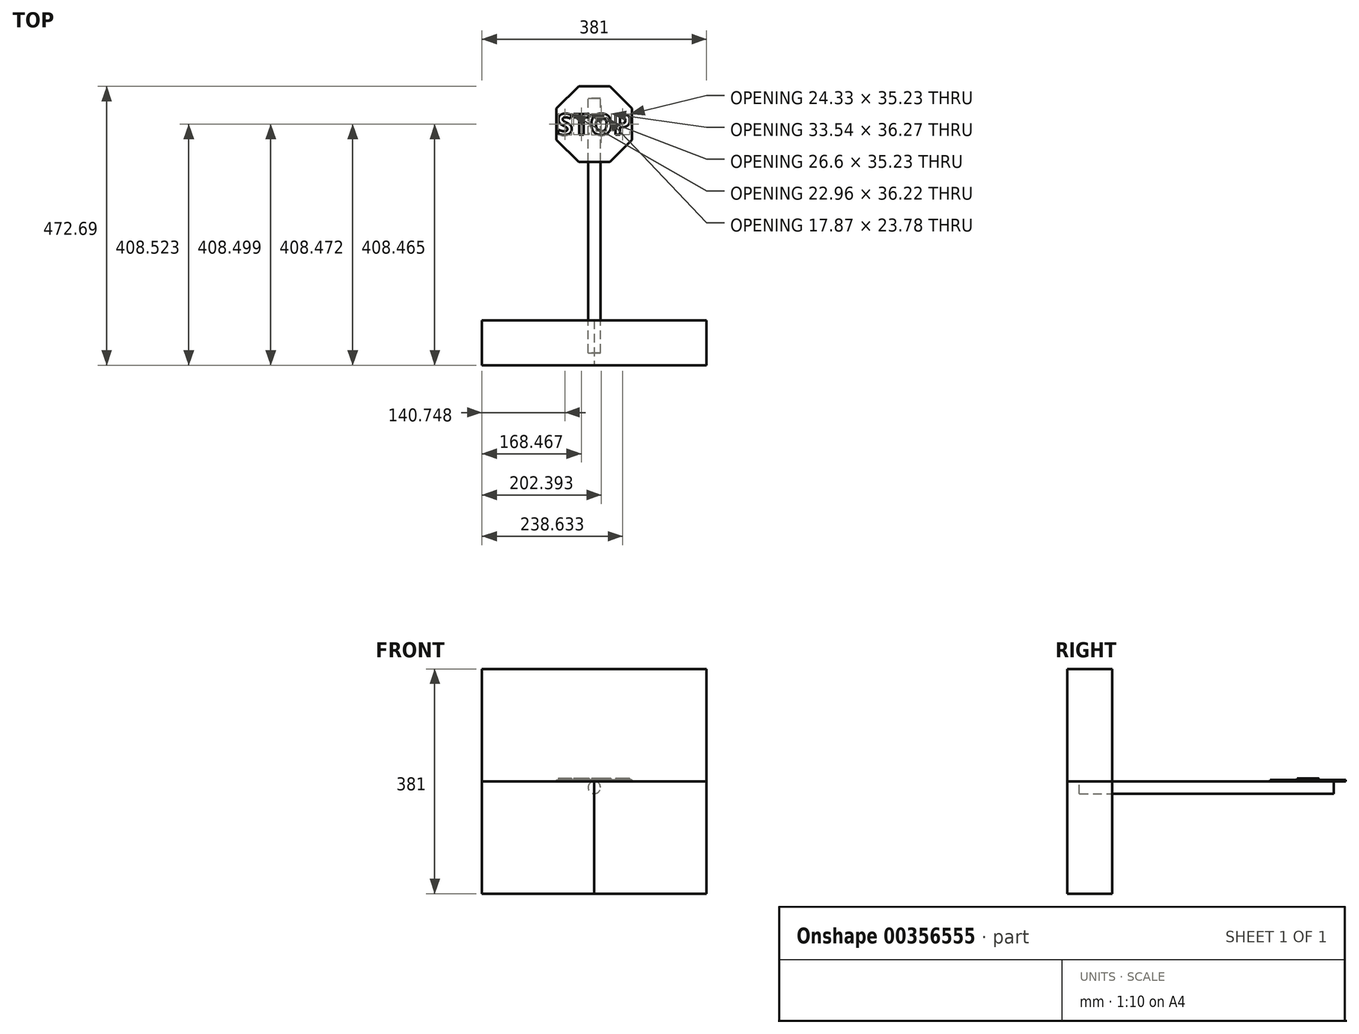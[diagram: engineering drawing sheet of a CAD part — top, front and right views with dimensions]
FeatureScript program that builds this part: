
annotation { "Feature Type Name" : "Feature", "Feature Type Description" : "" }
export const myFeature = defineFeature(function(context is Context, id is Id, definition is map)
    precondition{}
    {
        {
            var Q0;
            Q0=qCreatedBy(makeId("Top.planeOp"),FACE);
            var sketch = newSketch(context, id + "F0", { "sketchPlane" : qUnion([Q0])});
            skPoint(sketch, "E0.0.midPoint", {"position": v(0, -63.5) * mm});
            skText(sketch, "E1", { "text": "STOP\n\n", "fontName": "OpenSans-Bold.ttf"});
            skPoint(sketch, "E2.0.midPoint", {"position": v(-32.65, -98.94) * mm});
            skPoint(sketch, "E3.0.midPoint", {"position": v(-57.86, -79) * mm});
            skCircle(sketch, "E4.cCircle", {"center": v(0, -44.07) * mm, "radius": 64.08 * mm, "construction": true});
            skLineSegment(sketch, "E4.0", {"start": v(26.54, -108.15) * mm, "end": v(-26.54, -108.15) * mm});
            skLineSegment(sketch, "E4.1", {"start": v(-26.54, -108.15) * mm, "end": v(-64.08, -70.61) * mm});
            skLineSegment(sketch, "E4.2", {"start": v(-64.08, -70.61) * mm, "end": v(-64.08, -17.52) * mm});
            skLineSegment(sketch, "E4.3", {"start": v(-64.08, -17.52) * mm, "end": v(-26.54, 20.01) * mm});
            skLineSegment(sketch, "E4.4", {"start": v(-26.54, 20.01) * mm, "end": v(26.54, 20.01) * mm});
            skLineSegment(sketch, "E4.5", {"start": v(26.54, 20.01) * mm, "end": v(64.08, -17.52) * mm});
            skLineSegment(sketch, "E4.6", {"start": v(64.08, -17.52) * mm, "end": v(64.08, -70.61) * mm});
            skLineSegment(sketch, "E4.7", {"start": v(64.08, -70.61) * mm, "end": v(26.54, -108.15) * mm});
            skPoint(sketch, "E4.0.midPoint", {"position": v(0, -108.15) * mm});
            const initialGuessF0  = {"E1": [-0.0635, -0.06183, 1, 0, 0.03553]};
            skSetInitialGuess(sketch, initialGuessF0);
            skSolve(sketch);
        }
        {
            var Q0;
            Q0=makeQuery(id+"F0.imprint","IMPRINT",FACE,{"disambiguationData":[TD([[makeQuery(id+"F0.imprint","IMPRINT",EDGE,{"derivedFrom":sQuery(id+"F0.wireOp",EDGE,"E1.sketch_text.stroke-28")}),-1.0]])]});
            var Q1;
            Q1=makeQuery(id+"F0.imprint","IMPRINT",FACE,{"disambiguationData":[TD([[makeQuery(id+"F0.imprint","IMPRINT",EDGE,{"derivedFrom":sQuery(id+"F0.wireOp",EDGE,"E1.sketch_text.stroke-0")}),-1.0]])]});
            var Q2;
            Q2=makeQuery(id+"F0.imprint","IMPRINT",FACE,{"disambiguationData":[TD([[makeQuery(id+"F0.imprint","IMPRINT",EDGE,{"derivedFrom":sQuery(id+"F0.wireOp",EDGE,"E1.sketch_text.stroke-36")}),-1.0]])]});
            var Q3;
            Q3=makeQuery(id+"F0.imprint","IMPRINT",FACE,{"disambiguationData":[TD([[makeQuery(id+"F0.imprint","IMPRINT",EDGE,{"derivedFrom":sQuery(id+"F0.wireOp",EDGE,"E1.sketch_text.stroke-50")}),-1.0]])]});
            extrude(context, id + "F1", {"entities" : qUnion([Q0, Q1, Q2, Q3]), "depth" : 5.08 * mm});
        }
        {
            var Q0;
            Q0 = qSketchRegion(id + "F0", true);
            var Q1;
            Q1=makeQuery(id+"F0.imprint","IMPRINT",FACE,{"disambiguationData":[TD([[makeQuery(id+"F0.imprint","IMPRINT",EDGE,{"derivedFrom":sQuery(id+"F0.wireOp",EDGE,"E1.sketch_text.stroke-44")}),1.0]])]});
            var Q2;
            Q2=makeQuery(id+"F0.imprint","IMPRINT",FACE,{"disambiguationData":[TD([[makeQuery(id+"F0.imprint","IMPRINT",EDGE,{"derivedFrom":sQuery(id+"F0.wireOp",EDGE,"E1.sketch_text.stroke-50")}),1.0]])]});
            extrude(context, id + "F2", {"entities" : qUnion([Q0, Q1, Q2]), "depth" : 2.54 * mm});
        }
        {
            var Q0;
            Q0=qCreatedBy(makeId("Front.planeOp"),FACE);
            var sketch = newSketch(context, id + "F3", { "sketchPlane" : qUnion([Q0])});
            skCircle(sketch, "E5", {"center": v(0, -10.48) * mm, "radius": 10.48 * mm});
            skSolve(sketch);
        }
        {
            var Q0;
            Q0=makeQuery(id+"F3.imprint","IMPRINT",FACE,{"disambiguationData":[TD([[makeQuery(id+"F3.imprint","IMPRINT",EDGE,{"derivedFrom":sQuery(id+"F3.wireOp",EDGE,"E5")}),1.0]])]});
            extrude(context, id + "F4", {"entities" : qUnion([Q0]), "depth" : 431.8 * mm, "offsetDistance" : 25.4 * mm});
        }
        {
            var Q0;
            Q0=qCreatedBy(makeId("Top.planeOp"),FACE);
            var sketch = newSketch(context, id + "F5", { "sketchPlane" : qUnion([Q0])});
            skLineSegment(sketch, "E6.bottom", {"start": v(0, -376.48) * mm, "end": v(-190.5, -376.48) * mm});
            skLineSegment(sketch, "E6.top", {"start": v(0, -452.68) * mm, "end": v(-190.5, -452.68) * mm});
            skLineSegment(sketch, "E6.left", {"start": v(0, -376.48) * mm, "end": v(0, -452.68) * mm});
            skLineSegment(sketch, "E6.right", {"start": v(-190.5, -376.48) * mm, "end": v(-190.5, -452.68) * mm});
            skLineSegment(sketch, "E7.bottom", {"start": v(-48.93, -376.48) * mm, "end": v(0, -376.48) * mm});
            skLineSegment(sketch, "E7.top", {"start": v(-48.93, -452.68) * mm, "end": v(0, -452.68) * mm});
            skLineSegment(sketch, "E7.right", {"start": v(-48.93, -376.48) * mm, "end": v(-48.93, -452.68) * mm});
            skLineSegment(sketch, "E8.bottom", {"start": v(0, -376.48) * mm, "end": v(190.5, -376.48) * mm});
            skLineSegment(sketch, "E8.top", {"start": v(0, -452.68) * mm, "end": v(190.5, -452.68) * mm});
            skLineSegment(sketch, "E8.right", {"start": v(190.5, -376.48) * mm, "end": v(190.5, -452.68) * mm});
            skSolve(sketch);
        }
        {
            var Q0;
            Q0=makeQuery(id+"F5.imprint","IMPRINT",FACE,{"disambiguationData":[TD([[makeQuery(id+"F5.imprint","IMPRINT",EDGE,{"derivedFrom":sQuery(id+"F5.wireOp",EDGE,"E6.left")}),1.0]])]});
            var Q1;
            {var subQ2=sQuery(id+"F5.wireOp",EDGE,"E6.left");Q1=makeQuery(id+"F5.imprint","IMPRINT",FACE,{"disambiguationData":[TD([[makeQuery(id+"F5.imprint","IMPRINT",EDGE,{"derivedFrom":subQ2}),-1.0]])]});}
            var Q2;
            {var subQ2=sQuery(id+"F5.wireOp",EDGE,"E6.right");Q2=makeQuery(id+"F5.imprint","IMPRINT",FACE,{"disambiguationData":[TD([[makeQuery(id+"F5.imprint","IMPRINT",EDGE,{"derivedFrom":subQ2}),1.0]])]});}
            extrude(context, id + "F6", {"entities" : qUnion([Q0, Q1, Q2]), "operationType" : NewBodyOperationType.ADD, "depth" : 190.5 * mm, "offsetDistance" : 25.4 * mm});
        }
        {
            var Q0;
            Q0=makeQuery(id+"F6.opExtrude","CAP_FACE",FACE,{"disambiguationData":[OSD([sQuery(id+"F5.wireOp",EDGE,"E6.bottom"),sQuery(id+"F5.wireOp",EDGE,"E6.top"),sQuery(id+"F5.wireOp",EDGE,"E6.right"),sQuery(id+"F5.wireOp",EDGE,"E8.bottom"),sQuery(id+"F5.wireOp",EDGE,"E8.top"),sQuery(id+"F5.wireOp",EDGE,"E8.right")])],"isStart":true});
            var Q1;
            {var subQ2=sQuery(id+"F5.wireOp",EDGE,"E6.right");Q1=makeQuery(id+"F5.imprint","IMPRINT",FACE,{"disambiguationData":[TD([[makeQuery(id+"F5.imprint","IMPRINT",EDGE,{"derivedFrom":subQ2}),1.0]])]});}
            var Q2;
            {var subQ2=sQuery(id+"F5.wireOp",EDGE,"E6.left");Q2=makeQuery(id+"F5.imprint","IMPRINT",FACE,{"disambiguationData":[TD([[makeQuery(id+"F5.imprint","IMPRINT",EDGE,{"derivedFrom":subQ2}),-1.0]])]});}
            extrude(context, id + "F7", {"entities" : qUnion([Q0, Q1, Q2]), "depth" : 190.5 * mm, "offsetDistance" : 25.4 * mm});
        }
    });
